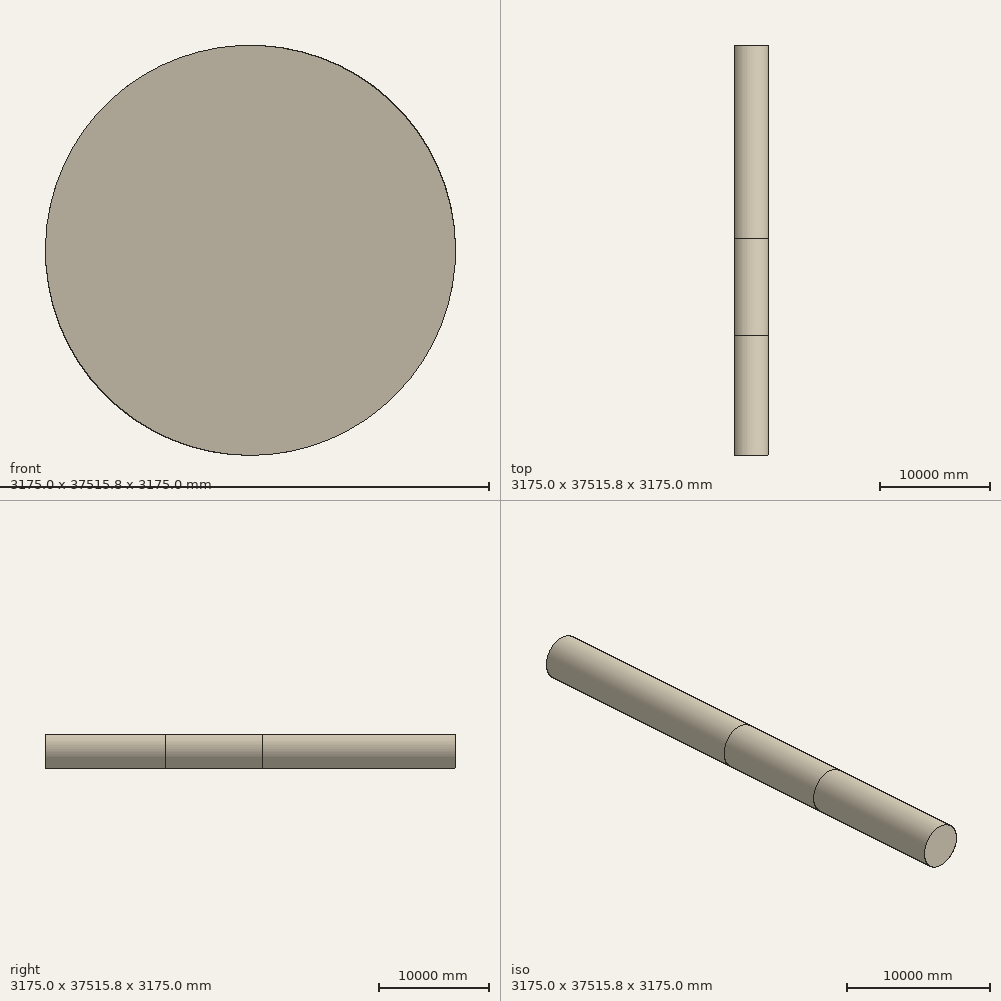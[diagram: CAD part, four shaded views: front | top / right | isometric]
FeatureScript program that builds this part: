
annotation { "Feature Type Name" : "Feature", "Feature Type Description" : "" }
export const myFeature = defineFeature(function(context is Context, id is Id, definition is map)
    precondition{}
    {
        {
            var Q0;
            Q0=qCreatedBy(makeId("Front.planeOp"),FACE);
            var sketch = newSketch(context, id + "F0", { "sketchPlane" : qUnion([Q0])});
            skCircle(sketch, "E0", {"center": v(0, 0) * mm, "radius": 1587.5 * mm});
            skSolve(sketch);
        }
        {
            var Q0;
            Q0 = qSketchRegion(id + "F0", true);
            extrude(context, id + "F1", {"entities" : qUnion([Q0]), "depth" : 10998.2 * mm, "offsetDistance" : 25.4 * mm});
        }
        {
            var Q0;
            Q0=makeQuery(id+"F1.opExtrude","CAP_FACE",FACE,{"disambiguationData":[OSD([sQuery(id+"F0.wireOp",EDGE,"E0")])],"isStart":true});
            var sketch = newSketch(context, id + "F2", { "sketchPlane" : qUnion([Q0])});
            skCircle(sketch, "E1", {"center": v(0, 0) * mm, "radius": 1587.5 * mm});
            skCircle(sketch, "E2", {"center": v(0, 0) * mm, "radius": 889 * mm});
            skSolve(sketch);
        }
        {
            var Q0;
            Q0 = qSketchRegion(id + "F2", true);
            extrude(context, id + "F3", {"entities" : qUnion([Q0]), "depth" : 8890 * mm, "offsetDistance" : 25.4 * mm});
        }
        {
            var Q0;
            Q0=makeQuery(id+"F3.opExtrude","CAP_FACE",FACE,{"disambiguationData":[OSD([sQuery(id+"F2.wireOp",EDGE,"E1"),sQuery(id+"F2.wireOp",EDGE,"E2")])],"isStart":false});
            var sketch = newSketch(context, id + "F4", { "sketchPlane" : qUnion([Q0])});
            skCircle(sketch, "E3", {"center": v(0, 0) * mm, "radius": 1587.5 * mm});
            skSolve(sketch);
        }
        {
            var Q0;
            Q0 = qSketchRegion(id + "F4", true);
            extrude(context, id + "F5", {"entities" : qUnion([Q0]), "depth" : 17627.6 * mm, "offsetDistance" : 25.4 * mm});
        }
    });
